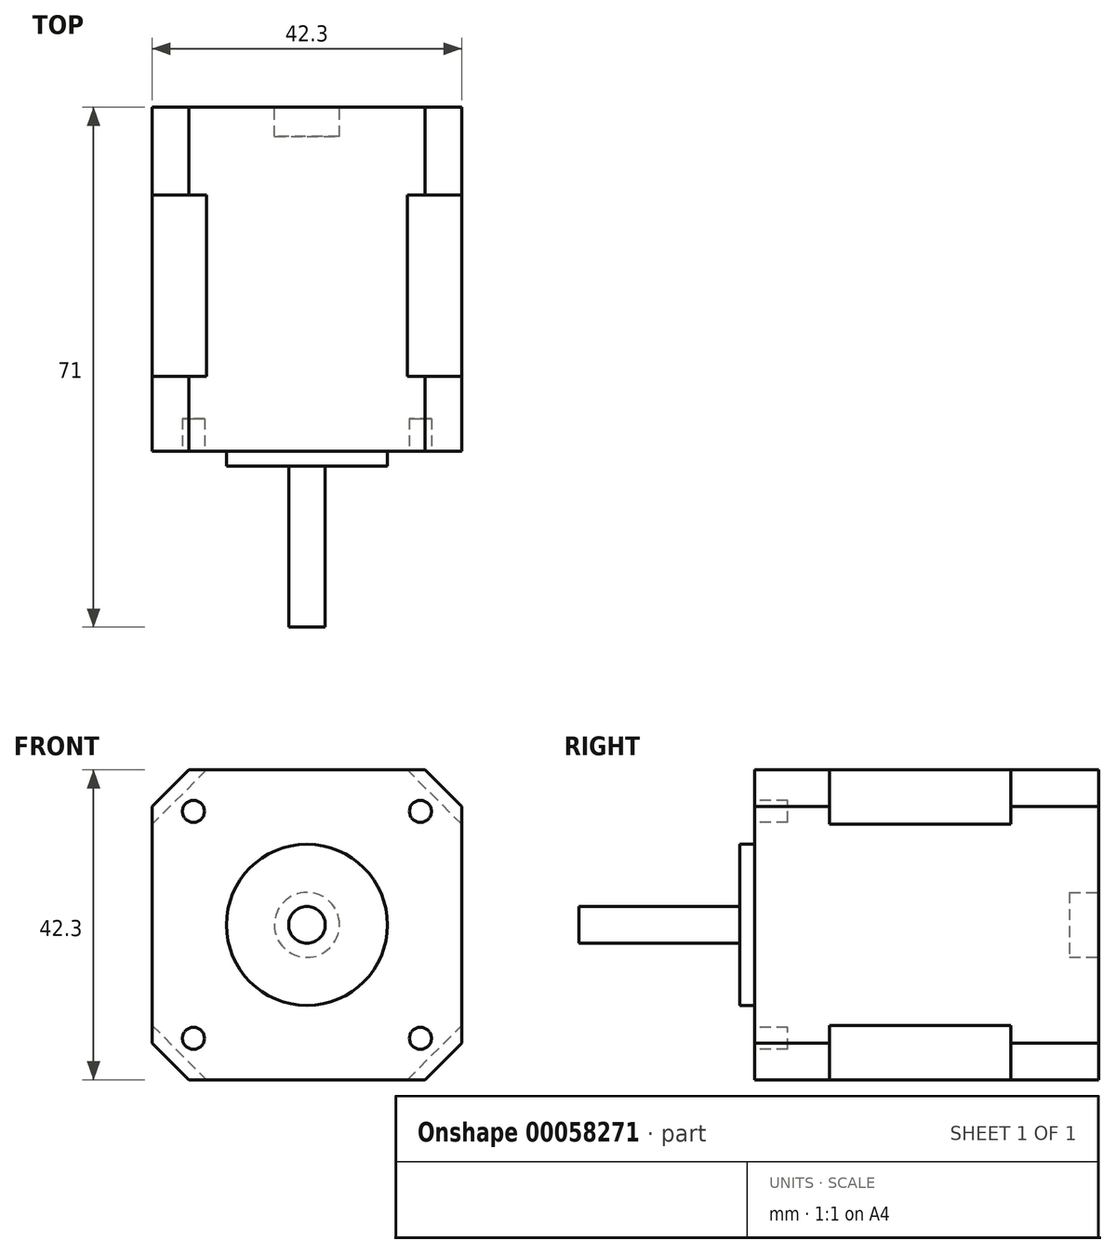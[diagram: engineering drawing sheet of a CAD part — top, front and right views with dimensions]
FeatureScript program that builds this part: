
annotation { "Feature Type Name" : "Feature", "Feature Type Description" : "" }
export const myFeature = defineFeature(function(context is Context, id is Id, definition is map)
    precondition{}
    {
        {
            var Q0;
            Q0=qCreatedBy(makeId("Front.planeOp"),FACE);
            var sketch = newSketch(context, id + "F0", { "sketchPlane" : qUnion([Q0])});
            skLineSegment(sketch, "E0.rect.bottom", {"start": v(21.15, 21.15) * mm, "end": v(-21.15, 21.15) * mm});
            skLineSegment(sketch, "E0.rect.top", {"start": v(21.15, -21.15) * mm, "end": v(-21.15, -21.15) * mm});
            skLineSegment(sketch, "E0.rect.left", {"start": v(21.15, 21.15) * mm, "end": v(21.15, -21.15) * mm});
            skLineSegment(sketch, "E0.rect.right", {"start": v(-21.15, 21.15) * mm, "end": v(-21.15, -21.15) * mm});
            skPoint(sketch, "E0.rect.middle", {"position": v(0, 0) * mm});
            skSolve(sketch);
        }
        {
            var Q0;
            Q0=qSketchRegion(id+"F0",true);
            extrude(context, id + "F1", {"entities" : qUnion([Q0]), "depth" : 47 * mm});
        }
        {
            var Q0;
            Q0=makeQuery(id+"F1.opExtrude","CAP_FACE",FACE,{"disambiguationData":[OSD([sQuery(id+"F0.wireOp",EDGE,"E0.rect.bottom"),sQuery(id+"F0.wireOp",EDGE,"E0.rect.top"),sQuery(id+"F0.wireOp",EDGE,"E0.rect.left"),sQuery(id+"F0.wireOp",EDGE,"E0.rect.right")])],"isStart":false});
            var sketch = newSketch(context, id + "F2", { "sketchPlane" : qUnion([Q0])});
            skLineSegment(sketch, "E1", {"start": v(0, 21.15) * mm, "end": v(0, -21.15) * mm, "construction": true});
            skLineSegment(sketch, "E2", {"start": v(-21.15, 0) * mm, "end": v(21.15, 0) * mm, "construction": true});
            skLineSegment(sketch, "E3", {"start": v(-21.15, 21.15) * mm, "end": v(0, 0) * mm, "construction": true});
            skCircle(sketch, "E4", {"center": v(-15.5, 15.5) * mm, "radius": 1.5 * mm});
            skCircle(sketch, "E5.1.0", {"center": v(-15.5, -15.5) * mm, "radius": 1.5 * mm});
            skCircle(sketch, "E5.2.0", {"center": v(15.5, -15.5) * mm, "radius": 1.5 * mm});
            skPoint(sketch, "E5.center", {"position": v(0, 0) * mm});
            skCircle(sketch, "E6.1.3.0", {"center": v(15.5, 15.5) * mm, "radius": 1.5 * mm});
            skSolve(sketch);
        }
        {
            var Q0;
            Q0=qSketchRegion(id+"F2",true);
            extrude(context, id + "F3", {"entities" : qUnion([Q0]), "operationType" : NewBodyOperationType.REMOVE, "oppositeDirection" : true, "depth" : 4.5 * mm});
        }
        {
            var Q0;
            Q0=makeQuery(id+"F1.opExtrude","CAP_FACE",FACE,{"disambiguationData":[OSD([sQuery(id+"F0.wireOp",EDGE,"E0.rect.bottom"),sQuery(id+"F0.wireOp",EDGE,"E0.rect.top"),sQuery(id+"F0.wireOp",EDGE,"E0.rect.left"),sQuery(id+"F0.wireOp",EDGE,"E0.rect.right")])],"isStart":false});
            var sketch = newSketch(context, id + "F4", { "sketchPlane" : qUnion([Q0])});
            skLineSegment(sketch, "E7", {"start": v(0, 21.15) * mm, "end": v(0, -21.15) * mm, "construction": true});
            skCircle(sketch, "E8", {"center": v(0, 0) * mm, "radius": 11 * mm});
            skSolve(sketch);
        }
        {
            var Q0;
            Q0=qSketchRegion(id+"F4",true);
            extrude(context, id + "F5", {"entities" : qUnion([Q0]), "depth" : 2 * mm});
        }
        {
            var Q0;
            Q0=makeQuery(id+"F5.opExtrude","CAP_FACE",FACE,{"disambiguationData":[OSD([sQuery(id+"F4.wireOp",EDGE,"E8")])],"isStart":false});
            var sketch = newSketch(context, id + "F6", { "sketchPlane" : qUnion([Q0])});
            skCircle(sketch, "E9", {"center": v(0, 0) * mm, "radius": 2.5 * mm});
            skSolve(sketch);
        }
        {
            var Q0;
            Q0=qSketchRegion(id+"F6",true);
            extrude(context, id + "F7", {"entities" : qUnion([Q0]), "operationType" : NewBodyOperationType.ADD, "depth" : 22 * mm});
        }
        {
            var Q0;
            Q0=makeQuery(id+"F1.opExtrude","SWEPT_EDGE",EDGE,{"disambiguationData":[OSD([sQuery(id+"F0.wireOp",EDGE,"E0.rect.bottom"),sQuery(id+"F0.wireOp",EDGE,"E0.rect.left")])]});
            var Q1;
            Q1=makeQuery(id+"F1.opExtrude","SWEPT_EDGE",EDGE,{"disambiguationData":[OSD([sQuery(id+"F0.wireOp",EDGE,"E0.rect.bottom"),sQuery(id+"F0.wireOp",EDGE,"E0.rect.right")])]});
            var Q2;
            Q2=makeQuery(id+"F1.opExtrude","SWEPT_EDGE",EDGE,{"disambiguationData":[OSD([sQuery(id+"F0.wireOp",EDGE,"E0.rect.top"),sQuery(id+"F0.wireOp",EDGE,"E0.rect.left")])]});
            var Q3;
            Q3=makeQuery(id+"F1.opExtrude","SWEPT_EDGE",EDGE,{"disambiguationData":[OSD([sQuery(id+"F0.wireOp",EDGE,"E0.rect.top"),sQuery(id+"F0.wireOp",EDGE,"E0.rect.right")])]});
            chamfer(context, id + "F8", {"entities" : qUnion([Q0, Q1, Q2, Q3]), "width" : 5 * mm, "tangentPropagation" : true});
        }
        {
            var Q0;
            Q0=makeQuery(id+"F1.opExtrude","CAP_FACE",FACE,{"disambiguationData":[OSD([sQuery(id+"F0.wireOp",EDGE,"E0.rect.bottom"),sQuery(id+"F0.wireOp",EDGE,"E0.rect.top"),sQuery(id+"F0.wireOp",EDGE,"E0.rect.left"),sQuery(id+"F0.wireOp",EDGE,"E0.rect.right")])],"isStart":true});
            cPlane(context, id + "F9", {"entities" : qUnion([Q0]), "cplaneType" : CPlaneType.OFFSET, "offset" : 12 * mm, "oppositeDirection" : true, "width" : 150 * mm, "height" : 150 * mm});
        }
        {
            var Q0;
            Q0=qCreatedBy(id+"F9.planeOp",FACE);
            var sketch = newSketch(context, id + "F10", { "sketchPlane" : qUnion([Q0])});
            skLineSegment(sketch, "E10.0", {"start": v(-16.15, 21.15) * mm, "end": v(16.15, 21.15) * mm, "construction": true});
            skLineSegment(sketch, "E10.1", {"start": v(-16.15, 21.15) * mm, "end": v(-21.15, 16.15) * mm});
            skLineSegment(sketch, "E10.2", {"start": v(-21.15, 16.15) * mm, "end": v(-21.15, -16.15) * mm, "construction": true});
            skLineSegment(sketch, "E11", {"start": v(-21.15, 13.73) * mm, "end": v(-13.73, 21.15) * mm});
            skLineSegment(sketch, "E12", {"start": v(-13.73, 21.15) * mm, "end": v(-16.15, 21.15) * mm});
            skLineSegment(sketch, "E13", {"start": v(-21.15, 16.15) * mm, "end": v(-21.15, 13.73) * mm});
            skLineSegment(sketch, "E14.1.0", {"start": v(-16.15, -21.15) * mm, "end": v(-13.73, -21.15) * mm});
            skLineSegment(sketch, "E14.1.1", {"start": v(-13.73, -21.15) * mm, "end": v(-21.15, -13.73) * mm});
            skLineSegment(sketch, "E14.1.2", {"start": v(-21.15, -13.73) * mm, "end": v(-21.15, -16.15) * mm});
            skLineSegment(sketch, "E14.1.3", {"start": v(-21.15, -16.15) * mm, "end": v(-16.15, -21.15) * mm});
            skLineSegment(sketch, "E14.2.0", {"start": v(21.15, -16.15) * mm, "end": v(21.15, -13.73) * mm});
            skLineSegment(sketch, "E14.2.1", {"start": v(21.15, -13.73) * mm, "end": v(13.73, -21.15) * mm});
            skLineSegment(sketch, "E14.2.2", {"start": v(13.73, -21.15) * mm, "end": v(16.15, -21.15) * mm});
            skLineSegment(sketch, "E14.2.3", {"start": v(16.15, -21.15) * mm, "end": v(21.15, -16.15) * mm});
            skPoint(sketch, "E14.center", {"position": v(0, 0) * mm});
            skLineSegment(sketch, "E15.2.3.0", {"start": v(16.15, 21.15) * mm, "end": v(13.73, 21.15) * mm});
            skLineSegment(sketch, "E15.3.3.0", {"start": v(13.73, 21.15) * mm, "end": v(21.15, 13.73) * mm});
            skLineSegment(sketch, "E15.6.3.0", {"start": v(21.15, 13.73) * mm, "end": v(21.15, 16.15) * mm});
            skLineSegment(sketch, "E15.9.3.0", {"start": v(21.15, 16.15) * mm, "end": v(16.15, 21.15) * mm});
            skSolve(sketch);
        }
        {
            var Q0;
            Q0=qSketchRegion(id+"F10",true);
            extrude(context, id + "F11", {"entities" : qUnion([Q0]), "operationType" : NewBodyOperationType.REMOVE, "oppositeDirection" : true, "depth" : 24.75 * mm});
        }
        {
            var Q0;
            Q0=makeQuery(id+"F1.opExtrude","CAP_FACE",FACE,{"disambiguationData":[OSD([sQuery(id+"F0.wireOp",EDGE,"E0.rect.bottom"),sQuery(id+"F0.wireOp",EDGE,"E0.rect.top"),sQuery(id+"F0.wireOp",EDGE,"E0.rect.left"),sQuery(id+"F0.wireOp",EDGE,"E0.rect.right")])],"isStart":true});
            var sketch = newSketch(context, id + "F12", { "sketchPlane" : qUnion([Q0])});
            skCircle(sketch, "E16", {"center": v(0, 0) * mm, "radius": 4.44 * mm});
            skSolve(sketch);
        }
        {
            var Q0;
            Q0=qSketchRegion(id+"F12",true);
            extrude(context, id + "F13", {"entities" : qUnion([Q0]), "operationType" : NewBodyOperationType.REMOVE, "oppositeDirection" : true, "depth" : 4 * mm});
        }
    });
